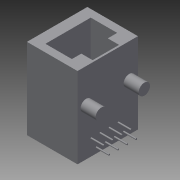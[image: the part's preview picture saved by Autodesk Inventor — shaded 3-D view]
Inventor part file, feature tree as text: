
AUTODESK INVENTOR PART (.ipt)
format: ipt  version: 2016 (Build 200138000, 138)  size: 142,336 bytes
history: native  units: in
note: dims shown in document units (in); Inventor stores cm internally (conversion verified against a paired STEP export)
features: extrude x4, sketch x4
ambient origin geometry x8: Origin, YZ Plane, XZ Plane, XY Plane, X Axis, Y Axis, Z Axis, Center Point
bodies: Solid1 (feature_tree)
feature tree (8):
  extrude  "Extrusion1"  Depth=0.6299in
  extrude  "Extrusion2"  Depth=0.4724in
  extrude  "Extrusion3"  Depth=0.2756in
  extrude  "Extrusion4"  Depth=0.2756in
  sketch  "Sketch1"  dims[d0=0.5276in d1=0.6299in]
  sketch  "Sketch2"  dims[d2=0.8425in d3=0.0in d4=0.4724in]
  sketch  "Sketch3"  dims[d5=0.2756in d6=0.2756in]
  sketch  "Sketch4"  dims[d7=0.1181in d8=0.2756in d9=0.0984in d10=0.0984in d11=0.0787in d12=0.0787in d13=0.1142in d14=0.4724in d15=0.0in d16=0.1181in d17=0.1181in d18=0.3543in d19=0.3543in d20=0.0906in d21=0.0906in d22=0.1575in d23=0.0in d24=0.0157in d25=0.0157in d26=0.1417in d27=0.0945in d28=0.0157in d29=0.0157in d30=0.0945in d31=0.0945in d32=0.0in d33=0.0in d34=0.0in d35=0.1654in d36=0.0551in d37=0.0157in d38=0.0157in d39=0.0157in d40=0.0157in d41=0.0551in d42=0.0945in d43=0.0945in d44=0.0945in d45=0.1339in d46=0.0in]
